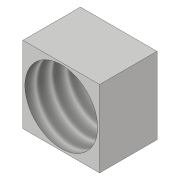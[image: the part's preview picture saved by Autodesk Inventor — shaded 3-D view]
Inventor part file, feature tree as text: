
AUTODESK INVENTOR PART (.ipt)
format: ipt  version: 2019 (Build 230136000, 136)  size: 94,720 bytes
history: native  units: in
note: dims shown in document units (in); Inventor stores cm internally (conversion verified against a paired STEP export)
features: extrude x2, sketch x2, thread x1
ambient origin geometry x8: Origin, YZ Plane, XZ Plane, XY Plane, X Axis, Y Axis, Z Axis, Center Point
bodies: Solid1 (feature_tree)
feature tree (5):
  extrude  "Extrusion1"  Depth=0.0787in
  extrude  "Extrusion2"  Depth=0.3937in
  thread  "Thread1"  [1 undecoded]
  sketch  "Sketch1"  dims[d0=0.0787in d1=0.0787in]
  sketch  "Sketch2"  dims[d2=0.0591in d3=0.0in d4=0.0748in d5=0.0in d6=0.0in d7=0.3937in d8=0.0in]
note: 1 required parameter value undecoded (feature->parameter linkage not recoverable at this tier; creation-order binding heuristic only, values carry confidence <= 0.55)
